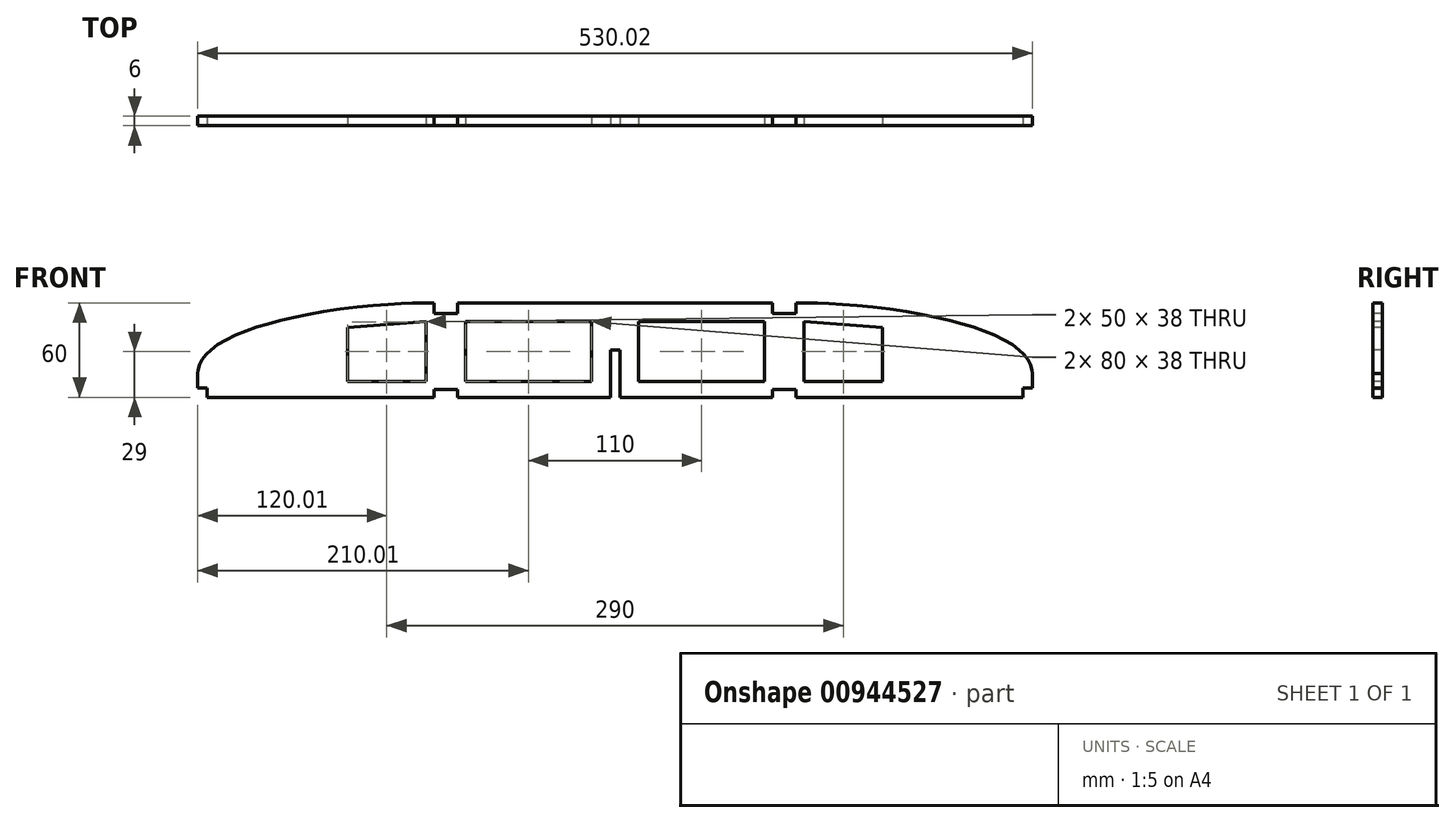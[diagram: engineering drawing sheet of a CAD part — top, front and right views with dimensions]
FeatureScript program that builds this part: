
annotation { "Feature Type Name" : "Feature", "Feature Type Description" : "" }
export const myFeature = defineFeature(function(context is Context, id is Id, definition is map)
    precondition{}
    {
        {
            var Q0;
            Q0=qCreatedBy(makeId("Front.planeOp"),FACE);
            var sketch = newSketch(context, id + "F0", { "sketchPlane" : qUnion([Q0])});
            skLineSegment(sketch, "E0.bottom", {"start": v(0, 0) * mm, "end": v(270, 0) * mm, "construction": true});
            skLineSegment(sketch, "E0.top", {"start": v(0, 70) * mm, "end": v(270, 70) * mm, "construction": true});
            skLineSegment(sketch, "E0.left", {"start": v(0, 0) * mm, "end": v(0, 70) * mm, "construction": true});
            skLineSegment(sketch, "E0.right", {"start": v(270, 0) * mm, "end": v(270, 70) * mm, "construction": true});
            skLineSegment(sketch, "E1", {"start": v(270, 0) * mm, "end": v(456.45, 0) * mm, "construction": true});
            skLineSegment(sketch, "E2", {"start": v(270, 70) * mm, "end": v(456.45, 0) * mm, "construction": true});
            skLineSegment(sketch, "E3", {"start": v(403.18, 20) * mm, "end": v(403.18, 0) * mm, "construction": true});
            skLineSegment(sketch, "E4", {"start": v(403.18, 20) * mm, "end": v(270, 20) * mm, "construction": true});
            skLineSegment(sketch, "E5", {"start": v(0, 70) * mm, "end": v(120, 70) * mm, "construction": true});
            skFitSpline(sketch, "E6", {"points": [v(120, 70) * mm, v(270, 20) * mm], "startDerivative": vector(90, 0) * mm, "endDerivative": vector(0, -121.92) * mm, "construction": true});
            skLineSegment(sketch, "E7", {"start": v(270, 20) * mm, "end": v(270, 0) * mm});
            skFitSpline(sketch, "E8.0", {"points": [v(120, 65) * mm, v(121.8, 65) * mm, v(126.17, 64.93) * mm, v(137.33, 64.45) * mm, v(155.03, 63.16) * mm, v(179.75, 60.22) * mm, v(201.16, 56.42) * mm, v(217.5, 52.47) * mm, v(229.04, 49.02) * mm, v(239.52, 45.09) * mm, v(248.62, 40.67) * mm, v(254.75, 36.64) * mm, v(258.62, 33.26) * mm, v(260.98, 30.68) * mm, v(262.8, 28.08) * mm, v(264.06, 25.47) * mm, v(264.82, 22.81) * mm, v(265, 20.96) * mm, v(265, 20) * mm]});
            skLineSegment(sketch, "E8.1", {"start": v(0, 65) * mm, "end": v(120, 65) * mm});
            skLineSegment(sketch, "E9", {"start": v(0, 5) * mm, "end": v(265, 5) * mm});
            skLineSegment(sketch, "E10", {"start": v(265, 5) * mm, "end": v(265, 20) * mm});
            skLineSegment(sketch, "E11", {"start": v(0, 65) * mm, "end": v(0, 5) * mm});
            skSolve(sketch);
        }
        {
            var Q0;
            Q0=makeQuery(id+"F0.imprint","IMPRINT",FACE,{"disambiguationData":[TD([[makeQuery(id+"F0.imprint","IMPRINT",EDGE,{"derivedFrom":sQuery(id+"F0.wireOp",EDGE,"E8.0")}),-1.0]])]});
            extrude(context, id + "F1", {"entities" : qUnion([Q0]), "depth" : 6 * mm, "offsetDistance" : 25 * mm});
        }
        {
            var Q0;
            Q0=makeQuery(id+"F1.opExtrude","CAP_FACE",FACE,{"disambiguationData":[OSD([sQuery(id+"F0.wireOp",EDGE,"E8.0"),sQuery(id+"F0.wireOp",EDGE,"E8.1"),sQuery(id+"F0.wireOp",EDGE,"E9"),sQuery(id+"F0.wireOp",EDGE,"E10"),sQuery(id+"F0.wireOp",EDGE,"E11")])],"isStart":false});
            var sketch = newSketch(context, id + "F2", { "sketchPlane" : qUnion([Q0])});
            skFitSpline(sketch, "E12.0", {"points": [v(120, 53) * mm, v(120.83, 53) * mm, v(122.69, 52.98) * mm, v(127.13, 52.88) * mm, v(133.88, 52.59) * mm, v(143.5, 51.97) * mm, v(154.3, 51.04) * mm, v(165.95, 49.77) * mm, v(178.11, 48.14) * mm, v(190.47, 46.13) * mm, v(202.68, 43.7) * mm, v(214.4, 40.87) * mm, v(225.26, 37.62) * mm, v(233.26, 34.61) * mm, v(238.83, 32.08) * mm, v(242.53, 30.14) * mm, v(245.18, 28.53) * mm, v(247, 27.27) * mm, v(248.63, 26.05) * mm, v(250.28, 24.6) * mm, v(251.64, 23.1) * mm, v(252.3, 22.11) * mm, v(252.63, 21.5) * mm, v(252.76, 21.2) * mm, v(252.84, 20.98) * mm, v(252.89, 20.84) * mm, v(252.92, 20.7) * mm, v(252.95, 20.57) * mm, v(252.97, 20.44) * mm, v(253, 20.26) * mm, v(253, 20.12) * mm, v(253, 20) * mm], "construction": true});
            skLineSegment(sketch, "E12.1", {"start": v(0, 53) * mm, "end": v(120, 53) * mm, "construction": true});
            skLineSegment(sketch, "E13", {"start": v(0, 15) * mm, "end": v(253, 15) * mm, "construction": true});
            skLineSegment(sketch, "E14", {"start": v(253, 20) * mm, "end": v(253, 15) * mm});
            skLineSegment(sketch, "E15.bottom", {"start": v(15, 53) * mm, "end": v(95, 53) * mm});
            skLineSegment(sketch, "E15.top", {"start": v(15, 15) * mm, "end": v(95, 15) * mm});
            skLineSegment(sketch, "E15.left", {"start": v(15, 53) * mm, "end": v(15, 15) * mm});
            skLineSegment(sketch, "E15.right", {"start": v(95, 53) * mm, "end": v(95, 15) * mm});
            skLineSegment(sketch, "E16", {"start": v(120, 53) * mm, "end": v(120, 15) * mm});
            skLineSegment(sketch, "E17", {"start": v(120, 15) * mm, "end": v(170, 15) * mm});
            skLineSegment(sketch, "E18", {"start": v(170, 15) * mm, "end": v(170, 49.21) * mm});
            skLineSegment(sketch, "E19", {"start": v(170, 49.21) * mm, "end": v(120, 53) * mm});
            skLineSegment(sketch, "E20", {"start": v(185, 47) * mm, "end": v(185, 15) * mm});
            skLineSegment(sketch, "E21", {"start": v(185, 15) * mm, "end": v(243.86, 15) * mm});
            skLineSegment(sketch, "E22", {"start": v(243.86, 15) * mm, "end": v(243.86, 29.32) * mm});
            skFitSpline(sketch, "E23", {"points": [v(120, 53) * mm, v(120.83, 53) * mm, v(122.69, 52.98) * mm, v(127.13, 52.88) * mm, v(133.88, 52.59) * mm, v(143.5, 51.97) * mm, v(154.3, 51.04) * mm, v(165.95, 49.77) * mm, v(178.11, 48.14) * mm, v(190.47, 46.13) * mm, v(202.68, 43.7) * mm, v(214.4, 40.87) * mm, v(225.26, 37.62) * mm, v(233.26, 34.61) * mm, v(238.83, 32.08) * mm, v(242.53, 30.14) * mm, v(245.18, 28.53) * mm, v(247, 27.27) * mm, v(248.63, 26.05) * mm, v(250.28, 24.6) * mm, v(251.64, 23.1) * mm, v(252.3, 22.11) * mm, v(252.63, 21.5) * mm, v(252.76, 21.2) * mm, v(252.84, 20.98) * mm, v(252.89, 20.84) * mm, v(252.92, 20.7) * mm, v(252.95, 20.57) * mm, v(252.97, 20.44) * mm, v(253, 20.26) * mm, v(253, 20.12) * mm, v(253, 20) * mm]});
            skFitSpline(sketch, "E24", {"points": [v(120, 53) * mm, v(120.83, 53) * mm, v(122.69, 52.98) * mm, v(127.13, 52.88) * mm, v(133.88, 52.59) * mm, v(143.5, 51.97) * mm, v(154.3, 51.04) * mm, v(165.95, 49.77) * mm, v(178.11, 48.14) * mm, v(190.47, 46.13) * mm, v(202.68, 43.7) * mm, v(214.4, 40.87) * mm, v(225.26, 37.62) * mm, v(233.26, 34.61) * mm, v(238.83, 32.08) * mm, v(242.53, 30.14) * mm, v(245.18, 28.53) * mm, v(247, 27.27) * mm, v(248.63, 26.05) * mm, v(250.28, 24.6) * mm, v(251.64, 23.1) * mm, v(252.3, 22.11) * mm, v(252.63, 21.5) * mm, v(252.76, 21.2) * mm, v(252.84, 20.98) * mm, v(252.89, 20.84) * mm, v(252.92, 20.7) * mm, v(252.95, 20.57) * mm, v(252.97, 20.44) * mm, v(253, 20.26) * mm, v(253, 20.12) * mm, v(253, 20) * mm], "construction": true});
            skSolve(sketch);
        }
        {
            var Q0;
            Q0 = qSketchRegion(id + "F2", true);
            extrude(context, id + "F3", {"entities" : qUnion([Q0]), "operationType" : NewBodyOperationType.REMOVE, "oppositeDirection" : true, "depth" : 25 * mm, "offsetDistance" : 25 * mm});
        }
        {
            var Q0;
            Q0=makeQuery(id+"F1.opExtrude","CAP_FACE",FACE,{"disambiguationData":[OSD([sQuery(id+"F0.wireOp",EDGE,"E8.0"),sQuery(id+"F0.wireOp",EDGE,"E8.1"),sQuery(id+"F0.wireOp",EDGE,"E9"),sQuery(id+"F0.wireOp",EDGE,"E10"),sQuery(id+"F0.wireOp",EDGE,"E11")])],"isStart":false});
            var sketch = newSketch(context, id + "F4", { "sketchPlane" : qUnion([Q0])});
            skLineSegment(sketch, "E25.bottom", {"start": v(265, 5) * mm, "end": v(259, 5) * mm});
            skLineSegment(sketch, "E25.top", {"start": v(265, 11) * mm, "end": v(259, 11) * mm});
            skLineSegment(sketch, "E25.left", {"start": v(265, 5) * mm, "end": v(265, 11) * mm});
            skLineSegment(sketch, "E25.right", {"start": v(259, 5) * mm, "end": v(259, 11) * mm});
            skLineSegment(sketch, "E26.bottom", {"start": v(0, 35) * mm, "end": v(3, 35) * mm});
            skLineSegment(sketch, "E26.top", {"start": v(0, 5) * mm, "end": v(3, 5) * mm});
            skLineSegment(sketch, "E26.left", {"start": v(0, 35) * mm, "end": v(0, 5) * mm});
            skLineSegment(sketch, "E26.right", {"start": v(3, 35) * mm, "end": v(3, 5) * mm});
            skLineSegment(sketch, "E27", {"start": v(100, 5) * mm, "end": v(100, 65) * mm, "construction": true});
            skLineSegment(sketch, "E28", {"start": v(115, 5) * mm, "end": v(115, 65) * mm, "construction": true});
            skLineSegment(sketch, "E29.bottom", {"start": v(100, 5) * mm, "end": v(115, 5) * mm});
            skLineSegment(sketch, "E29.top", {"start": v(100, 10) * mm, "end": v(115, 10) * mm});
            skLineSegment(sketch, "E29.left", {"start": v(100, 5) * mm, "end": v(100, 10) * mm});
            skLineSegment(sketch, "E29.right", {"start": v(115, 5) * mm, "end": v(115, 10) * mm});
            skLineSegment(sketch, "E30.bottom", {"start": v(100, 65) * mm, "end": v(115, 65) * mm});
            skLineSegment(sketch, "E30.top", {"start": v(100, 58.25) * mm, "end": v(115, 58.25) * mm});
            skLineSegment(sketch, "E30.left", {"start": v(100, 65) * mm, "end": v(100, 58.25) * mm});
            skLineSegment(sketch, "E30.right", {"start": v(115, 65) * mm, "end": v(115, 58.25) * mm});
            skSolve(sketch);
        }
        {
            var Q0;
            Q0 = qSketchRegion(id + "F4", true);
            extrude(context, id + "F5", {"entities" : qUnion([Q0]), "operationType" : NewBodyOperationType.REMOVE, "oppositeDirection" : true, "depth" : 25 * mm, "offsetDistance" : 25 * mm});
        }
        {
            var Q0;
            Q0=makeQuery(id+"F1.opExtrude","SWEPT_BODY",BODY,{"disambiguationData":[OSD([sQuery(id+"F0.wireOp",EDGE,"E8.0"),sQuery(id+"F0.wireOp",EDGE,"E8.1"),sQuery(id+"F0.wireOp",EDGE,"E9"),sQuery(id+"F0.wireOp",EDGE,"E10"),sQuery(id+"F0.wireOp",EDGE,"E11")])]});
            var Q1;
            Q1=qCreatedBy(makeId("Right.planeOp"),FACE);
            mirror(context, id + "F6", {"operationType" : NewBodyOperationType.ADD, "entities" : qUnion([Q0]), "mirrorPlane" : qUnion([Q1])});
        }
    });
